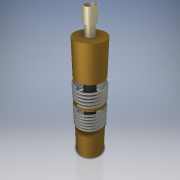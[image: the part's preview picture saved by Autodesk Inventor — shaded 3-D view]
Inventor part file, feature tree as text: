
AUTODESK INVENTOR PART (.ipt)
format: ipt  version: 2018 (Build 220112000, 112)  size: 351,232 bytes
history: native  units: in
note: dims shown in document units (in); Inventor stores cm internally (conversion verified against a paired STEP export)
features: sketch x9, extrude x6, helix x2, revolve x1
ambient origin geometry x8: Origin, YZ Plane, XZ Plane, XY Plane, X Axis, Y Axis, Z Axis, Center Point
bodies: Body1 (feature_tree)
feature tree (18):
  extrude  "Extrusion3"  Depth=0.5in
  extrude  "Extrusion4"  Depth=0.3in
  extrude  "Extrusion5"  Depth=0.03in
  extrude  "Extrusion6"  Depth=1.25in
  extrude  "Extrusion7"  Depth=0.5in
  helix  "Coil1"  [1 undecoded]
  extrude  "Extrusion8"  Depth=0.625in
  helix  "Coil2"  [1 undecoded]
  revolve  "Revolution1"  [1 undecoded]
  sketch  "Sketch3"  dims[d6=0.44in d7=0.5in]
  sketch  "Sketch4"  dims[d8=0.44in d9=0.0in d10=0.3in]
  sketch  "Sketch5"  dims[d11=0.1in d12=0.0in d13=0.03in]
  sketch  "Sketch6"  dims[d14=0.44in d15=0.0in d16=1.25in]
  sketch  "Sketch7"  dims[d17=1.5in d18=0.0in d19=0.5in d20=2.5in d21=0.0in]
  sketch  "Sketch8"  dims[d23=0.1in]
  sketch  "Sketch9"  dims[d24=0.15in d25=1.0in d26=4.7244in d27=0.0in d28=90.0deg d29=90.0deg d30=0.0in d31=0.0in d32=0.625in d33=1.25in]
  sketch  "Sketch11"  dims[d37=0.0in d38=0.0in d39=90.0deg d40=90.0deg d41=0.0in d42=4.7244in d43=0.75in d44=0.15in d45=0.625in d47=0.1in d48=0.25in d49=0.1in d50=0.65in d51=90.0deg d52=3.1in]
  sketch  "Sketch10"  dims[d34=1.25in d35=1.25in d36=0.0in]
note: 3 required parameter values undecoded (feature->parameter linkage not recoverable at this tier; creation-order binding heuristic only, values carry confidence <= 0.55)